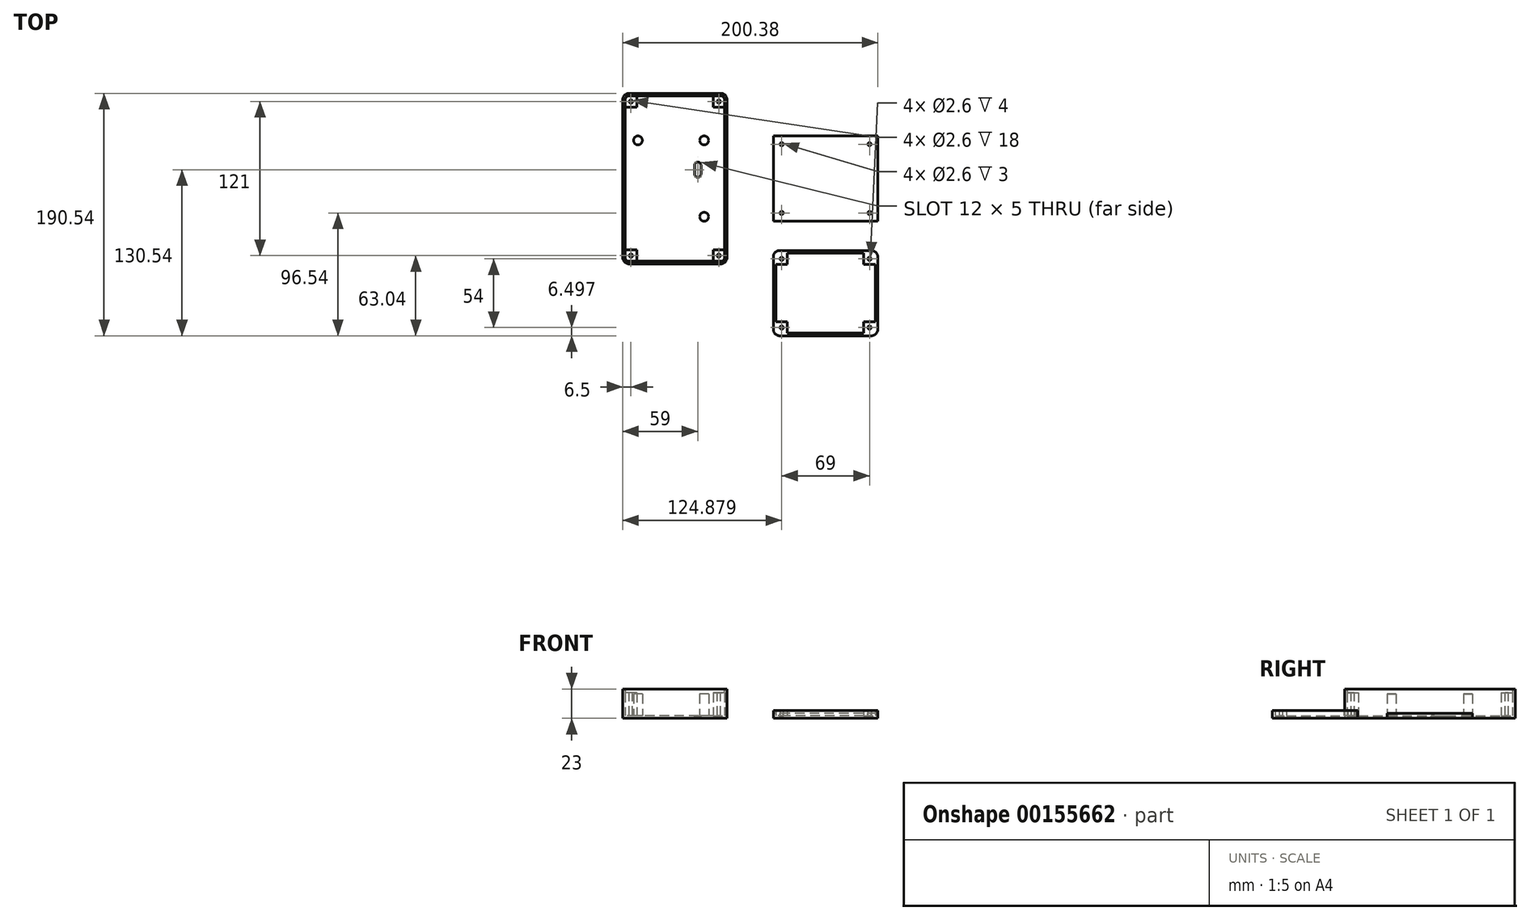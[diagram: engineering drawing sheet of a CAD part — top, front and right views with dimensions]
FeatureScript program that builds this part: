
annotation { "Feature Type Name" : "Feature", "Feature Type Description" : "" }
export const myFeature = defineFeature(function(context is Context, id is Id, definition is map)
    precondition{}
    {
        {
            var Q0;
            Q0=qCreatedBy(makeId("Top.planeOp"),FACE);
            var sketch = newSketch(context, id + "F0", { "sketchPlane" : qUnion([Q0])});
            skLineSegment(sketch, "E0.bottom", {"start": v(36, -67) * mm, "end": v(-36, -67) * mm});
            skLineSegment(sketch, "E0.top", {"start": v(36, 67) * mm, "end": v(-36, 67) * mm});
            skLineSegment(sketch, "E0.left", {"start": v(41, -62) * mm, "end": v(41, 62) * mm});
            skLineSegment(sketch, "E0.right", {"start": v(-41, -62) * mm, "end": v(-41, 62) * mm});
            skPoint(sketch, "E0.middle", {"position": v(0, 0) * mm});
            skPoint(sketch, "E1.visualSharp", {"position": v(-41, 67) * mm});
            skArc(sketch, "E1.filletArc", {"start": v(-36, 67) * mm, "mid": v(-39.54, 65.54) * mm, "end": v(-41, 62) * mm});
            skPoint(sketch, "E2.visualSharp", {"position": v(41, 67) * mm});
            skArc(sketch, "E2.filletArc", {"start": v(41, 62) * mm, "mid": v(39.54, 65.54) * mm, "end": v(36, 67) * mm});
            skPoint(sketch, "E3.visualSharp", {"position": v(41, -67) * mm});
            skArc(sketch, "E3.filletArc", {"start": v(36, -67) * mm, "mid": v(39.54, -65.54) * mm, "end": v(41, -62) * mm});
            skPoint(sketch, "E4.visualSharp", {"position": v(-41, -67) * mm});
            skArc(sketch, "E4.filletArc", {"start": v(-41, -62) * mm, "mid": v(-39.54, -65.54) * mm, "end": v(-36, -67) * mm});
            skSolve(sketch);
        }
        {
            var Q0;
            Q0 = qSketchRegion(id + "F0", true);
            extrude(context, id + "F1", {"entities" : qUnion([Q0]), "depth" : 23 * mm});
        }
        {
            var Q0;
            Q0=makeQuery(id+"F1.opExtrude","CAP_FACE",FACE,{"disambiguationData":[OSD([sQuery(id+"F0.wireOp",EDGE,"E0.bottom"),sQuery(id+"F0.wireOp",EDGE,"E0.top"),sQuery(id+"F0.wireOp",EDGE,"E0.left"),sQuery(id+"F0.wireOp",EDGE,"E0.right"),sQuery(id+"F0.wireOp",EDGE,"E1.filletArc"),sQuery(id+"F0.wireOp",EDGE,"E2.filletArc"),sQuery(id+"F0.wireOp",EDGE,"E3.filletArc"),sQuery(id+"F0.wireOp",EDGE,"E4.filletArc")])],"isStart":false});
            shell(context, id + "F2", {"entities" : qUnion([Q0]), "thickness" : 2 * mm});
        }
        {
            var Q0;
            Q0=makeQuery(id+"F2.opShell","OFFSET_FACE",FACE,{"disambiguationData":[OSD([sQuery(id+"F0.wireOp",EDGE,"E0.bottom"),sQuery(id+"F0.wireOp",EDGE,"E0.top"),sQuery(id+"F0.wireOp",EDGE,"E0.left"),sQuery(id+"F0.wireOp",EDGE,"E0.right"),sQuery(id+"F0.wireOp",EDGE,"E1.filletArc"),sQuery(id+"F0.wireOp",EDGE,"E2.filletArc"),sQuery(id+"F0.wireOp",EDGE,"E3.filletArc"),sQuery(id+"F0.wireOp",EDGE,"E4.filletArc")])]});
            var sketch = newSketch(context, id + "F3", { "sketchPlane" : qUnion([Q0])});
            skCircle(sketch, "E5", {"center": v(-29, 30) * mm, "radius": 3.5 * mm});
            skCircle(sketch, "E6", {"center": v(23, 30) * mm, "radius": 3.5 * mm});
            skCircle(sketch, "E7", {"center": v(23, -30) * mm, "radius": 3.5 * mm});
            skLineSegment(sketch, "E8.bottom", {"start": v(-30, 56) * mm, "end": v(-39, 56) * mm});
            skLineSegment(sketch, "E8.top", {"start": v(-30, 65) * mm, "end": v(-39, 65) * mm});
            skLineSegment(sketch, "E8.left", {"start": v(-30, 56) * mm, "end": v(-30, 65) * mm});
            skLineSegment(sketch, "E8.right", {"start": v(-39, 56) * mm, "end": v(-39, 65) * mm});
            skPoint(sketch, "E8.middle", {"position": v(-34.5, 60.5) * mm});
            skLineSegment(sketch, "E9.bottom", {"start": v(-30, -65) * mm, "end": v(-39, -65) * mm});
            skLineSegment(sketch, "E9.top", {"start": v(-30, -56) * mm, "end": v(-39, -56) * mm});
            skLineSegment(sketch, "E9.left", {"start": v(-30, -65) * mm, "end": v(-30, -56) * mm});
            skLineSegment(sketch, "E9.right", {"start": v(-39, -65) * mm, "end": v(-39, -56) * mm});
            skPoint(sketch, "E9.middle", {"position": v(-34.5, -60.5) * mm});
            skPoint(sketch, "E10.MirrorP", {"position": v(34.5, -60.5) * mm});
            skLineSegment(sketch, "E11.MirrorCS", {"start": v(39, -65) * mm, "end": v(39, -56) * mm});
            skLineSegment(sketch, "E12.MirrorCS", {"start": v(30, -65) * mm, "end": v(30, -56) * mm});
            skLineSegment(sketch, "E13.MirrorCS", {"start": v(30, -65) * mm, "end": v(39, -65) * mm});
            skLineSegment(sketch, "E14.MirrorCS", {"start": v(30, -56) * mm, "end": v(39, -56) * mm});
            skLineSegment(sketch, "E15.MirrorCS", {"start": v(39, 56) * mm, "end": v(39, 65) * mm});
            skLineSegment(sketch, "E16.MirrorCS", {"start": v(30, 56) * mm, "end": v(39, 56) * mm});
            skLineSegment(sketch, "E17.MirrorCS", {"start": v(30, 56) * mm, "end": v(30, 65) * mm});
            skLineSegment(sketch, "E18.MirrorCS", {"start": v(30, 65) * mm, "end": v(39, 65) * mm});
            skPoint(sketch, "E19.MirrorP", {"position": v(34.5, 60.5) * mm});
            skLineSegment(sketch, "E20.left", {"start": v(20.5, 3.5) * mm, "end": v(20.5, 10.5) * mm});
            skLineSegment(sketch, "E20.right", {"start": v(15.5, 3.5) * mm, "end": v(15.5, 10.5) * mm});
            skPoint(sketch, "E20.middle", {"position": v(18, 7) * mm});
            skArc(sketch, "E21", {"start": v(15.5, 10.5) * mm, "mid": v(18, 13) * mm, "end": v(20.5, 10.5) * mm});
            skArc(sketch, "E22", {"start": v(20.5, 3.5) * mm, "mid": v(18, 1) * mm, "end": v(15.5, 3.5) * mm});
            skSolve(sketch);
        }
        {
            var Q0;
            {var subQ3=sQuery(id+"F3.wireOp",EDGE,"E8.bottom");Q0=makeQuery(id+"F3.imprint","IMPRINT",FACE,{"disambiguationData":[TD([[makeQuery(id+"F3.imprint","IMPRINT",EDGE,{"derivedFrom":subQ3}),-1.0]])]});}
            var Q1;
            {var subQ6=sQuery(id+"F3.wireOp",EDGE,"E16.MirrorCS");Q1=makeQuery(id+"F3.imprint","IMPRINT",FACE,{"disambiguationData":[TD([[makeQuery(id+"F3.imprint","IMPRINT",EDGE,{"derivedFrom":subQ6}),1.0]])]});}
            var Q2;
            {var subQ1=sQuery(id+"F3.wireOp",EDGE,"E9.top");Q2=makeQuery(id+"F3.imprint","IMPRINT",FACE,{"disambiguationData":[TD([[makeQuery(id+"F3.imprint","IMPRINT",EDGE,{"derivedFrom":subQ1}),1.0]])]});}
            var Q3;
            {var subQ3=sQuery(id+"F3.wireOp",EDGE,"E12.MirrorCS");Q3=makeQuery(id+"F3.imprint","IMPRINT",FACE,{"disambiguationData":[TD([[makeQuery(id+"F3.imprint","IMPRINT",EDGE,{"derivedFrom":subQ3}),-1.0]])]});}
            extrude(context, id + "F4", {"entities" : qUnion([Q0, Q1, Q2, Q3]), "operationType" : NewBodyOperationType.ADD, "depth" : 18 * mm});
        }
        {
            var Q0;
            Q0=makeQuery(id+"F3.imprint","IMPRINT",FACE,{"disambiguationData":[TD([[makeQuery(id+"F3.imprint","IMPRINT",EDGE,{"derivedFrom":sQuery(id+"F3.wireOp",EDGE,"E5")}),1.0]])]});
            var Q1;
            Q1=makeQuery(id+"F3.imprint","IMPRINT",FACE,{"disambiguationData":[TD([[makeQuery(id+"F3.imprint","IMPRINT",EDGE,{"derivedFrom":sQuery(id+"F3.wireOp",EDGE,"E6")}),1.0]])]});
            var Q2;
            Q2=makeQuery(id+"F3.imprint","IMPRINT",FACE,{"disambiguationData":[TD([[makeQuery(id+"F3.imprint","IMPRINT",EDGE,{"derivedFrom":sQuery(id+"F3.wireOp",EDGE,"E7")}),1.0]])]});
            extrude(context, id + "F5", {"entities" : qUnion([Q0, Q1, Q2]), "operationType" : NewBodyOperationType.ADD, "depth" : 17 * mm});
        }
        {
            var Q0;
            Q0=makeQuery(id+"F3.imprint","IMPRINT",FACE,{"disambiguationData":[TD([[makeQuery(id+"F3.imprint","IMPRINT",EDGE,{"derivedFrom":sQuery(id+"F3.wireOp",EDGE,"E20.left")}),1.0]])]});
            extrude(context, id + "F6", {"entities" : qUnion([Q0]), "operationType" : NewBodyOperationType.REMOVE, "oppositeDirection" : true, "depth" : 2 * mm});
        }
        {
            var Q0;
            Q0=makeQuery(id+"F4.opExtrude","CAP_FACE",FACE,{"disambiguationData":[OSD([sQuery(id+"F0.wireOp",EDGE,"E1.filletArc"),sQuery(id+"F3.wireOp",EDGE,"E8.bottom"),sQuery(id+"F3.wireOp",EDGE,"E8.top"),sQuery(id+"F3.wireOp",EDGE,"E8.left"),sQuery(id+"F3.wireOp",EDGE,"E8.right")])],"isStart":false});
            var sketch = newSketch(context, id + "F7", { "sketchPlane" : qUnion([Q0])});
            skCircle(sketch, "E23", {"center": v(-34.5, 60.5) * mm, "radius": 1.3 * mm});
            skCircle(sketch, "E24", {"center": v(-34.5, -60.5) * mm, "radius": 1.3 * mm});
            skCircle(sketch, "E25", {"center": v(34.5, 60.5) * mm, "radius": 1.3 * mm});
            skCircle(sketch, "E26", {"center": v(34.5, -60.5) * mm, "radius": 1.3 * mm});
            skSolve(sketch);
        }
        {
            var Q0;
            Q0 = qSketchRegion(id + "F7", true);
            extrude(context, id + "F8", {"entities" : qUnion([Q0]), "operationType" : NewBodyOperationType.REMOVE, "oppositeDirection" : true, "depth" : 18 * mm});
        }
        {
            var Q0;
            Q0=qCreatedBy(makeId("Top.planeOp"),FACE);
            var sketch = newSketch(context, id + "F9", { "sketchPlane" : qUnion([Q0])});
            skLineSegment(sketch, "E27.bottom", {"start": v(159.38, 33.5) * mm, "end": v(77.38, 33.5) * mm});
            skLineSegment(sketch, "E27.top", {"start": v(159.38, -33.5) * mm, "end": v(77.38, -33.5) * mm});
            skLineSegment(sketch, "E27.left", {"start": v(159.38, 33.5) * mm, "end": v(159.38, -33.5) * mm});
            skLineSegment(sketch, "E27.right", {"start": v(77.38, 33.5) * mm, "end": v(77.38, -33.5) * mm});
            skPoint(sketch, "E27.middle", {"position": v(118.38, 0) * mm});
            skLineSegment(sketch, "E28.bottom", {"start": v(154.38, -123.54) * mm, "end": v(82.38, -123.54) * mm});
            skLineSegment(sketch, "E28.top", {"start": v(154.38, -56.54) * mm, "end": v(82.38, -56.54) * mm});
            skLineSegment(sketch, "E28.left", {"start": v(159.38, -118.54) * mm, "end": v(159.38, -61.54) * mm});
            skLineSegment(sketch, "E28.right", {"start": v(77.38, -118.54) * mm, "end": v(77.38, -61.54) * mm});
            skPoint(sketch, "E28.middle", {"position": v(118.38, -90.04) * mm});
            skPoint(sketch, "E29.visualSharp", {"position": v(77.38, -56.54) * mm});
            skArc(sketch, "E29.filletArc", {"start": v(82.38, -56.54) * mm, "mid": v(78.84, -58) * mm, "end": v(77.38, -61.54) * mm});
            skPoint(sketch, "E30.visualSharp", {"position": v(159.38, -56.54) * mm});
            skArc(sketch, "E30.filletArc", {"start": v(159.38, -61.54) * mm, "mid": v(157.91, -58) * mm, "end": v(154.38, -56.54) * mm});
            skPoint(sketch, "E31.visualSharp", {"position": v(159.38, -123.54) * mm});
            skArc(sketch, "E31.filletArc", {"start": v(154.38, -123.54) * mm, "mid": v(157.91, -122.08) * mm, "end": v(159.38, -118.54) * mm});
            skPoint(sketch, "E32.visualSharp", {"position": v(77.38, -123.54) * mm});
            skArc(sketch, "E32.filletArc", {"start": v(77.38, -118.54) * mm, "mid": v(78.84, -122.08) * mm, "end": v(82.38, -123.54) * mm});
            skSolve(sketch);
        }
        {
            var Q0;
            Q0=makeQuery(id+"F9.imprint","IMPRINT",FACE,{"disambiguationData":[TD([[makeQuery(id+"F9.imprint","IMPRINT",EDGE,{"derivedFrom":sQuery(id+"F9.wireOp",EDGE,"E27.bottom")}),1.0]])]});
            extrude(context, id + "F10", {"entities" : qUnion([Q0]), "depth" : 4 * mm});
        }
        {
            var Q0;
            Q0=makeQuery(id+"F9.imprint","IMPRINT",FACE,{"disambiguationData":[TD([[makeQuery(id+"F9.imprint","IMPRINT",EDGE,{"derivedFrom":sQuery(id+"F9.wireOp",EDGE,"E28.bottom")}),-1.0]])]});
            extrude(context, id + "F11", {"entities" : qUnion([Q0]), "depth" : 6 * mm});
        }
        {
            var Q0;
            Q0=makeQuery(id+"F11.opExtrude","CAP_FACE",FACE,{"disambiguationData":[OSD([sQuery(id+"F9.wireOp",EDGE,"E28.bottom"),sQuery(id+"F9.wireOp",EDGE,"E28.top"),sQuery(id+"F9.wireOp",EDGE,"E28.left"),sQuery(id+"F9.wireOp",EDGE,"E28.right"),sQuery(id+"F9.wireOp",EDGE,"E29.filletArc"),sQuery(id+"F9.wireOp",EDGE,"E30.filletArc"),sQuery(id+"F9.wireOp",EDGE,"E31.filletArc"),sQuery(id+"F9.wireOp",EDGE,"E32.filletArc")])],"isStart":false});
            shell(context, id + "F12", {"entities" : qUnion([Q0]), "thickness" : 2 * mm});
        }
        {
            var Q0;
            Q0=makeQuery(id+"F10.opExtrude","CAP_FACE",FACE,{"disambiguationData":[OSD([sQuery(id+"F9.wireOp",EDGE,"E27.bottom"),sQuery(id+"F9.wireOp",EDGE,"E27.top"),sQuery(id+"F9.wireOp",EDGE,"E27.left"),sQuery(id+"F9.wireOp",EDGE,"E27.right")])],"isStart":false});
            var sketch = newSketch(context, id + "F13", { "sketchPlane" : qUnion([Q0])});
            skCircle(sketch, "E33", {"center": v(83.88, 27) * mm, "radius": 1.3 * mm});
            skCircle(sketch, "E34", {"center": v(152.88, 27) * mm, "radius": 1.3 * mm});
            skCircle(sketch, "E35", {"center": v(83.88, -27) * mm, "radius": 1.3 * mm});
            skCircle(sketch, "E36", {"center": v(152.88, -27) * mm, "radius": 1.3 * mm});
            skSolve(sketch);
        }
        {
            var Q0;
            Q0 = qSketchRegion(id + "F13", true);
            extrude(context, id + "F14", {"entities" : qUnion([Q0]), "operationType" : NewBodyOperationType.REMOVE, "oppositeDirection" : true, "depth" : 3 * mm});
        }
        {
            var Q0;
            Q0=makeQuery(id+"F12.opShell","OFFSET_FACE",FACE,{"disambiguationData":[OSD([sQuery(id+"F9.wireOp",EDGE,"E28.bottom"),sQuery(id+"F9.wireOp",EDGE,"E28.top"),sQuery(id+"F9.wireOp",EDGE,"E28.left"),sQuery(id+"F9.wireOp",EDGE,"E28.right"),sQuery(id+"F9.wireOp",EDGE,"E29.filletArc"),sQuery(id+"F9.wireOp",EDGE,"E30.filletArc"),sQuery(id+"F9.wireOp",EDGE,"E31.filletArc"),sQuery(id+"F9.wireOp",EDGE,"E32.filletArc")])]});
            var sketch = newSketch(context, id + "F15", { "sketchPlane" : qUnion([Q0])});
            skCircle(sketch, "E37", {"center": v(83.88, -63.04) * mm, "radius": 1.3 * mm});
            skCircle(sketch, "E38", {"center": v(152.88, -63.04) * mm, "radius": 1.3 * mm});
            skCircle(sketch, "E39", {"center": v(83.88, -117.04) * mm, "radius": 1.3 * mm});
            skCircle(sketch, "E40", {"center": v(152.88, -117.04) * mm, "radius": 1.3 * mm});
            skLineSegment(sketch, "E41.bottom", {"start": v(88.38, -58.54) * mm, "end": v(79.38, -58.54) * mm});
            skLineSegment(sketch, "E41.top", {"start": v(88.38, -67.54) * mm, "end": v(79.38, -67.54) * mm});
            skLineSegment(sketch, "E41.left", {"start": v(88.38, -58.54) * mm, "end": v(88.38, -67.54) * mm});
            skLineSegment(sketch, "E41.right", {"start": v(79.38, -58.54) * mm, "end": v(79.38, -67.54) * mm});
            skLineSegment(sketch, "E42.bottom", {"start": v(148.38, -58.54) * mm, "end": v(157.38, -58.54) * mm});
            skLineSegment(sketch, "E42.top", {"start": v(148.38, -67.54) * mm, "end": v(157.38, -67.54) * mm});
            skLineSegment(sketch, "E42.left", {"start": v(148.38, -58.54) * mm, "end": v(148.38, -67.54) * mm});
            skLineSegment(sketch, "E42.right", {"start": v(157.38, -58.54) * mm, "end": v(157.38, -67.54) * mm});
            skLineSegment(sketch, "E43.bottom", {"start": v(88.38, -121.54) * mm, "end": v(79.38, -121.54) * mm});
            skLineSegment(sketch, "E43.top", {"start": v(88.38, -112.54) * mm, "end": v(79.38, -112.54) * mm});
            skLineSegment(sketch, "E43.left", {"start": v(88.38, -121.54) * mm, "end": v(88.38, -112.54) * mm});
            skLineSegment(sketch, "E43.right", {"start": v(79.38, -121.54) * mm, "end": v(79.38, -112.54) * mm});
            skLineSegment(sketch, "E44.bottom", {"start": v(148.38, -121.54) * mm, "end": v(157.38, -121.54) * mm});
            skLineSegment(sketch, "E44.top", {"start": v(148.38, -112.54) * mm, "end": v(157.38, -112.54) * mm});
            skLineSegment(sketch, "E44.left", {"start": v(148.38, -121.54) * mm, "end": v(148.38, -112.54) * mm});
            skLineSegment(sketch, "E44.right", {"start": v(157.38, -121.54) * mm, "end": v(157.38, -112.54) * mm});
            skSolve(sketch);
        }
        {
            var Q0;
            Q0=makeQuery(id+"F15.imprint","IMPRINT",FACE,{"disambiguationData":[TD([[makeQuery(id+"F15.imprint","IMPRINT",EDGE,{"derivedFrom":sQuery(id+"F15.wireOp",EDGE,"E39")}),-1.0]])]});
            var Q1;
            Q1=makeQuery(id+"F15.imprint","IMPRINT",FACE,{"disambiguationData":[TD([[makeQuery(id+"F15.imprint","IMPRINT",EDGE,{"derivedFrom":sQuery(id+"F15.wireOp",EDGE,"E37")}),-1.0]])]});
            var Q2;
            Q2=makeQuery(id+"F15.imprint","IMPRINT",FACE,{"disambiguationData":[TD([[makeQuery(id+"F15.imprint","IMPRINT",EDGE,{"derivedFrom":sQuery(id+"F15.wireOp",EDGE,"E38")}),-1.0]])]});
            var Q3;
            Q3=makeQuery(id+"F15.imprint","IMPRINT",FACE,{"disambiguationData":[TD([[makeQuery(id+"F15.imprint","IMPRINT",EDGE,{"derivedFrom":sQuery(id+"F15.wireOp",EDGE,"E40")}),-1.0]])]});
            extrude(context, id + "F16", {"entities" : qUnion([Q0, Q1, Q2, Q3]), "operationType" : NewBodyOperationType.ADD, "depth" : 4 * mm});
        }
    });
